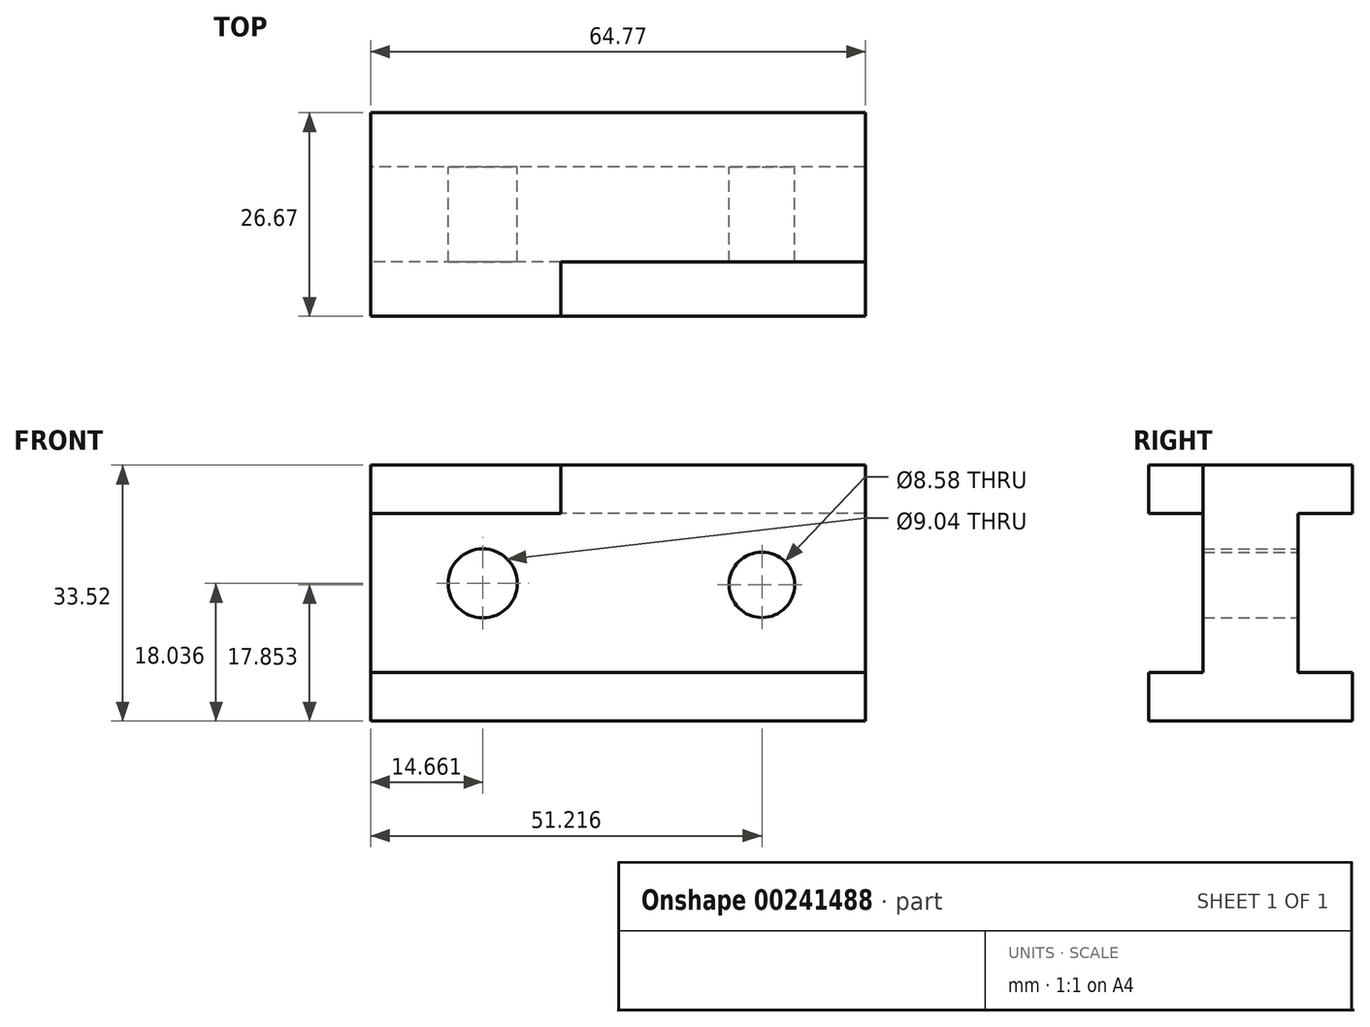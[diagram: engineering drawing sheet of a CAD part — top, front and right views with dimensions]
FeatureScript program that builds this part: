
annotation { "Feature Type Name" : "Feature", "Feature Type Description" : "" }
export const myFeature = defineFeature(function(context is Context, id is Id, definition is map)
    precondition{}
    {
        {
            var Q0;
            Q0=qCreatedBy(makeId("Right.planeOp"),FACE);
            var sketch = newSketch(context, id + "F0", { "sketchPlane" : qUnion([Q0])});
            skLineSegment(sketch, "E0.bottom", {"start": v(-5, 3.73) * mm, "end": v(7.45, 3.73) * mm});
            skLineSegment(sketch, "E0.top", {"start": v(-5, -23.46) * mm, "end": v(7.45, -23.46) * mm});
            skLineSegment(sketch, "E0.left", {"start": v(-5, 3.73) * mm, "end": v(-5, -23.46) * mm});
            skLineSegment(sketch, "E0.right", {"start": v(7.45, 3.73) * mm, "end": v(7.45, -23.46) * mm});
            skLineSegment(sketch, "E1.bottom", {"start": v(-12.1, -23.44) * mm, "end": v(14.56, -23.44) * mm});
            skLineSegment(sketch, "E1.top", {"start": v(-12.1, -29.79) * mm, "end": v(14.56, -29.79) * mm});
            skLineSegment(sketch, "E1.left", {"start": v(-12.1, -23.44) * mm, "end": v(-12.1, -29.79) * mm});
            skLineSegment(sketch, "E1.right", {"start": v(14.56, -23.44) * mm, "end": v(14.56, -29.79) * mm});
            skLineSegment(sketch, "E2.bottom", {"start": v(-5, 3.73) * mm, "end": v(-12.1, 3.73) * mm});
            skLineSegment(sketch, "E2.top", {"start": v(-5, -2.62) * mm, "end": v(-12.1, -2.62) * mm});
            skLineSegment(sketch, "E2.left", {"start": v(-5, 3.73) * mm, "end": v(-5, -2.62) * mm});
            skLineSegment(sketch, "E2.right", {"start": v(-12.1, 3.73) * mm, "end": v(-12.1, -2.62) * mm});
            skLineSegment(sketch, "E3.bottom", {"start": v(7.45, 3.73) * mm, "end": v(14.56, 3.73) * mm});
            skLineSegment(sketch, "E3.top", {"start": v(7.45, -2.62) * mm, "end": v(14.56, -2.62) * mm});
            skLineSegment(sketch, "E3.left", {"start": v(7.45, 3.73) * mm, "end": v(7.45, -2.62) * mm});
            skLineSegment(sketch, "E3.right", {"start": v(14.56, 3.73) * mm, "end": v(14.56, -2.62) * mm});
            skSolve(sketch);
        }
        {
            var Q0;
            Q0=makeQuery(id+"F0.imprint","IMPRINT",FACE,{"disambiguationData":[TD([[makeQuery(id+"F0.imprint","IMPRINT",EDGE,{"derivedFrom":sQuery(id+"F0.wireOp",EDGE,"E2.bottom")}),1.0]])]});
            extrude(context, id + "F1", {"entities" : qUnion([Q0]), "depth" : 24.9 * mm});
        }
        {
            var Q0;
            Q0=makeQuery(id+"F0.imprint","IMPRINT",FACE,{"disambiguationData":[TD([[makeQuery(id+"F0.imprint","IMPRINT",EDGE,{"derivedFrom":sQuery(id+"F0.wireOp",EDGE,"E3.bottom")}),-1.0]])]});
            var Q1;
            Q1=makeQuery(id+"F0.imprint","IMPRINT",FACE,{"disambiguationData":[TD([[makeQuery(id+"F0.imprint","IMPRINT",EDGE,{"derivedFrom":sQuery(id+"F0.wireOp",EDGE,"E0.bottom")}),-1.0]])]});
            var Q2;
            {var subQ0=sQuery(id+"F0.wireOp",EDGE,"E0.top");Q2=makeQuery(id+"F0.imprint","IMPRINT",FACE,{"disambiguationData":[TD([[makeQuery(id+"F0.imprint","IMPRINT",EDGE,{"derivedFrom":subQ0}),1.0]])]});}
            var Q3;
            Q3=makeQuery(id+"F1.opExtrude","SWEPT_FACE",FACE,{"disambiguationData":[OSD([sQuery(id+"F0.wireOp",EDGE,"E2.left")])]});
            var Q4;
            {var subQ5=sQuery(id+"F0.wireOp",EDGE,"E0.top");Q4=makeQuery(id+"F0.imprint","IMPRINT",FACE,{"disambiguationData":[TD([[makeQuery(id+"F0.imprint","IMPRINT",EDGE,{"derivedFrom":subQ5}),-1.0]])]});}
            extrude(context, id + "F2", {"entities" : qUnion([Q0, Q1, Q2, Q3, Q4]), "depth" : 64.77 * mm});
        }
        {
            var Q0;
            Q0=makeQuery(id+"F0.imprint","IMPRINT",FACE,{"disambiguationData":[TD([[makeQuery(id+"F0.imprint","IMPRINT",EDGE,{"derivedFrom":sQuery(id+"F0.wireOp",EDGE,"E3.bottom")}),-1.0]])]});
            var Q1;
            Q1=makeQuery(id+"F0.imprint","IMPRINT",FACE,{"disambiguationData":[TD([[makeQuery(id+"F0.imprint","IMPRINT",EDGE,{"derivedFrom":sQuery(id+"F0.wireOp",EDGE,"E0.bottom")}),-1.0]])]});
            var Q2;
            {var subQ5=sQuery(id+"F0.wireOp",EDGE,"E0.top");Q2=makeQuery(id+"F0.imprint","IMPRINT",FACE,{"disambiguationData":[TD([[makeQuery(id+"F0.imprint","IMPRINT",EDGE,{"derivedFrom":subQ5}),-1.0]])]});}
            extrude(context, id + "F3", {"entities" : qUnion([Q0, Q1, Q2]), "operationType" : NewBodyOperationType.ADD, "depth" : 64.77 * mm});
        }
        {
            var Q0;
            Q0=qCreatedBy(makeId("Front.planeOp"),FACE);
            var sketch = newSketch(context, id + "F4", { "sketchPlane" : qUnion([Q0])});
            skCircle(sketch, "E4", {"center": v(14.66, -11.75) * mm, "radius": 4.52 * mm});
            skCircle(sketch, "E5", {"center": v(51.22, -11.94) * mm, "radius": 4.3 * mm});
            skSolve(sketch);
        }
        {
            var Q0;
            Q0 = qSketchRegion(id + "F4", true);
            extrude(context, id + "F5", {"entities" : qUnion([Q0]), "operationType" : NewBodyOperationType.REMOVE, "depth" : 122.43 * mm, "hasSecondDirection" : true, "secondDirectionOppositeDirection" : true, "secondDirectionDepth" : 71.63 * mm});
        }
    });
